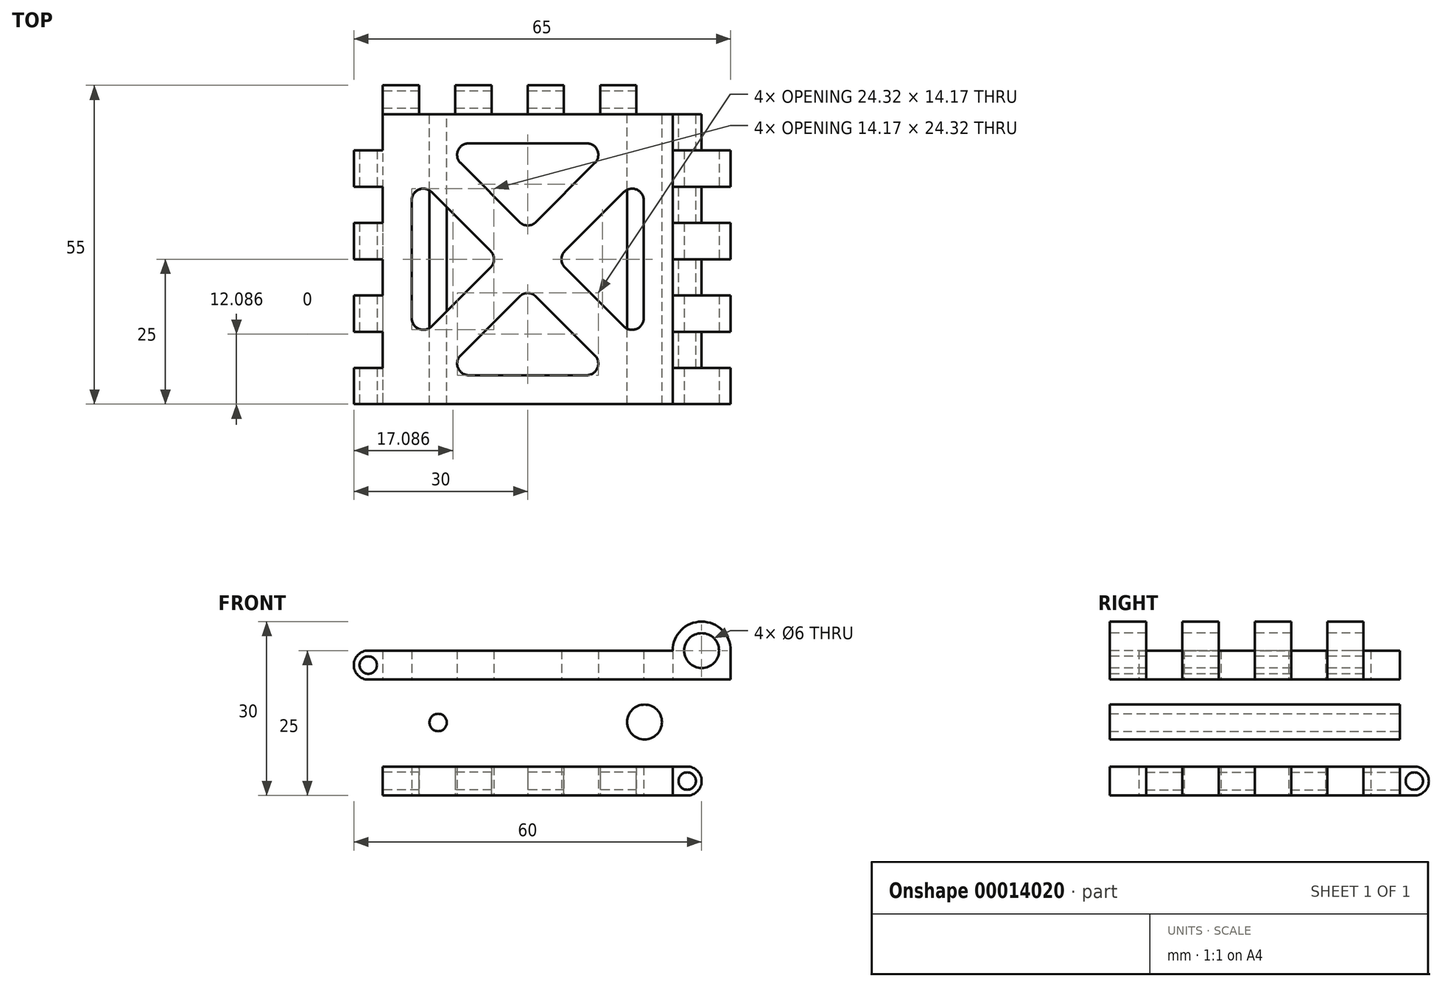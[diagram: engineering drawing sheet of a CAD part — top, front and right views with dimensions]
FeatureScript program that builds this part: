
annotation { "Feature Type Name" : "Feature", "Feature Type Description" : "" }
export const myFeature = defineFeature(function(context is Context, id is Id, definition is map)
    precondition{}
    {
        {
            var Q0;
            Q0=qCreatedBy(makeId("Top.planeOp"),FACE);
            var sketch = newSketch(context, id + "F0", { "sketchPlane" : qUnion([Q0])});
            skLineSegment(sketch, "E0.bottom", {"start": v(-25, 25) * mm, "end": v(25, 25) * mm});
            skLineSegment(sketch, "E0.top", {"start": v(-25, -25) * mm, "end": v(25, -25) * mm});
            skLineSegment(sketch, "E0.left", {"start": v(-25, 25) * mm, "end": v(-25, -25) * mm});
            skLineSegment(sketch, "E0.right", {"start": v(25, 25) * mm, "end": v(25, -25) * mm});
            skLineSegment(sketch, "E1", {"start": v(-25, 25) * mm, "end": v(25, -25) * mm, "construction": true});
            skLineSegment(sketch, "E2.top", {"start": v(-25, 35) * mm, "end": v(-18.75, 35) * mm});
            skLineSegment(sketch, "E2.left", {"start": v(-25, 25) * mm, "end": v(-25, 35) * mm});
            skLineSegment(sketch, "E2.right", {"start": v(25, 25) * mm, "end": v(25, 35) * mm});
            skLineSegment(sketch, "E3.bottom", {"start": v(25, 25) * mm, "end": v(35, 25) * mm});
            skLineSegment(sketch, "E3.top", {"start": v(25, -25) * mm, "end": v(35, -25) * mm});
            skLineSegment(sketch, "E3.right", {"start": v(35, 25) * mm, "end": v(35, 18.75) * mm});
            skLineSegment(sketch, "E4.bottom", {"start": v(25, -25) * mm, "end": v(-25, -25) * mm});
            skLineSegment(sketch, "E4.top", {"start": v(25, -35) * mm, "end": v(18.75, -35) * mm});
            skLineSegment(sketch, "E4.left", {"start": v(25, -25) * mm, "end": v(25, -35) * mm});
            skLineSegment(sketch, "E4.right", {"start": v(-25, -25) * mm, "end": v(-25, -35) * mm});
            skLineSegment(sketch, "E5", {"start": v(0, 35) * mm, "end": v(6.25, 35) * mm});
            skLineSegment(sketch, "E6", {"start": v(-12.5, 35) * mm, "end": v(-6.25, 35) * mm});
            skLineSegment(sketch, "E7", {"start": v(-18.75, 35) * mm, "end": v(-12.5, 35) * mm});
            skLineSegment(sketch, "E8", {"start": v(-6.25, 35) * mm, "end": v(0, 35) * mm});
            skLineSegment(sketch, "E9", {"start": v(12.5, 35) * mm, "end": v(18.75, 35) * mm});
            skLineSegment(sketch, "E10", {"start": v(6.25, 35) * mm, "end": v(12.5, 35) * mm});
            skLineSegment(sketch, "E11", {"start": v(18.75, 35) * mm, "end": v(25, 35) * mm});
            skLineSegment(sketch, "E12", {"start": v(35, 0) * mm, "end": v(35, -6.25) * mm});
            skLineSegment(sketch, "E13", {"start": v(35, 12.5) * mm, "end": v(35, 6.25) * mm});
            skLineSegment(sketch, "E14", {"start": v(35, 18.75) * mm, "end": v(35, 12.5) * mm});
            skLineSegment(sketch, "E15", {"start": v(35, 6.25) * mm, "end": v(35, 0) * mm});
            skLineSegment(sketch, "E16", {"start": v(35, -12.5) * mm, "end": v(35, -18.75) * mm});
            skLineSegment(sketch, "E17", {"start": v(35, -6.25) * mm, "end": v(35, -12.5) * mm});
            skLineSegment(sketch, "E18", {"start": v(35, -18.75) * mm, "end": v(35, -25) * mm});
            skLineSegment(sketch, "E19", {"start": v(0, -35) * mm, "end": v(-6.25, -35) * mm});
            skLineSegment(sketch, "E20", {"start": v(12.5, -35) * mm, "end": v(6.25, -35) * mm});
            skLineSegment(sketch, "E21", {"start": v(-12.5, -35) * mm, "end": v(-18.75, -35) * mm});
            skLineSegment(sketch, "E22", {"start": v(-18.75, -35) * mm, "end": v(-25, -35) * mm});
            skLineSegment(sketch, "E23", {"start": v(-6.25, -35) * mm, "end": v(-12.5, -35) * mm});
            skLineSegment(sketch, "E24", {"start": v(6.25, -35) * mm, "end": v(0, -35) * mm});
            skLineSegment(sketch, "E25", {"start": v(18.75, -35) * mm, "end": v(12.5, -35) * mm});
            skLineSegment(sketch, "E26.bottom", {"start": v(-25, 25) * mm, "end": v(-35, 25) * mm});
            skLineSegment(sketch, "E26.top", {"start": v(-25, -25) * mm, "end": v(-35, -25) * mm});
            skLineSegment(sketch, "E26.right", {"start": v(-35, 25) * mm, "end": v(-35, 18.75) * mm});
            skLineSegment(sketch, "E27", {"start": v(-35, 0) * mm, "end": v(-35, -6.25) * mm});
            skLineSegment(sketch, "E28", {"start": v(-35, 12.5) * mm, "end": v(-35, 6.25) * mm});
            skLineSegment(sketch, "E29", {"start": v(-35, -12.5) * mm, "end": v(-35, -18.75) * mm});
            skLineSegment(sketch, "E30", {"start": v(-35, -18.75) * mm, "end": v(-35, -25) * mm});
            skLineSegment(sketch, "E31", {"start": v(-35, -6.25) * mm, "end": v(-35, -12.5) * mm});
            skLineSegment(sketch, "E32", {"start": v(-35, 6.25) * mm, "end": v(-35, 0) * mm});
            skLineSegment(sketch, "E33", {"start": v(-35, 18.75) * mm, "end": v(-35, 12.5) * mm});
            skLineSegment(sketch, "E34", {"start": v(-18.75, 35) * mm, "end": v(-18.75, 25) * mm});
            skLineSegment(sketch, "E35", {"start": v(-12.5, -35) * mm, "end": v(-12.5, -25) * mm});
            skLineSegment(sketch, "E36", {"start": v(-6.25, 35) * mm, "end": v(-6.25, 25) * mm});
            skLineSegment(sketch, "E37", {"start": v(0, -35) * mm, "end": v(0, -25) * mm});
            skLineSegment(sketch, "E38", {"start": v(6.25, 35) * mm, "end": v(6.25, 25) * mm});
            skLineSegment(sketch, "E39", {"start": v(12.5, -35) * mm, "end": v(12.5, -25) * mm});
            skLineSegment(sketch, "E40", {"start": v(18.75, 35) * mm, "end": v(18.75, 25) * mm});
            skLineSegment(sketch, "E41", {"start": v(35, -18.75) * mm, "end": v(25, -18.75) * mm});
            skLineSegment(sketch, "E42", {"start": v(-35, -12.5) * mm, "end": v(-25, -12.5) * mm});
            skLineSegment(sketch, "E43", {"start": v(35, -6.25) * mm, "end": v(25, -6.25) * mm});
            skLineSegment(sketch, "E44", {"start": v(-35, 0) * mm, "end": v(-25, 0) * mm});
            skLineSegment(sketch, "E45", {"start": v(35, 6.25) * mm, "end": v(25, 6.25) * mm});
            skLineSegment(sketch, "E46", {"start": v(-35, 12.5) * mm, "end": v(-25, 12.5) * mm});
            skLineSegment(sketch, "E47", {"start": v(35, 18.75) * mm, "end": v(25, 18.75) * mm});
            skLineSegment(sketch, "E48.trimOffspring", {"start": v(-25, 18.75) * mm, "end": v(-35, 18.75) * mm});
            skLineSegment(sketch, "E49.trimOffspring", {"start": v(25, 12.5) * mm, "end": v(35, 12.5) * mm});
            skLineSegment(sketch, "E50.trimOffspring", {"start": v(25, 0) * mm, "end": v(35, 0) * mm});
            skLineSegment(sketch, "E51.trimOffspring", {"start": v(25, -12.5) * mm, "end": v(35, -12.5) * mm});
            skLineSegment(sketch, "E52.trimOffspring", {"start": v(18.75, -25) * mm, "end": v(18.75, -35) * mm});
            skLineSegment(sketch, "E53.trimOffspring", {"start": v(6.25, -25) * mm, "end": v(6.25, -35) * mm});
            skLineSegment(sketch, "E54.trimOffspring", {"start": v(-6.25, -25) * mm, "end": v(-6.25, -35) * mm});
            skLineSegment(sketch, "E55.trimOffspring", {"start": v(-18.75, -25) * mm, "end": v(-18.75, -35) * mm});
            skLineSegment(sketch, "E56.trimOffspring", {"start": v(-25, -18.75) * mm, "end": v(-35, -18.75) * mm});
            skLineSegment(sketch, "E57.trimOffspring", {"start": v(-25, -6.25) * mm, "end": v(-35, -6.25) * mm});
            skLineSegment(sketch, "E58.trimOffspring", {"start": v(-25, 6.25) * mm, "end": v(-35, 6.25) * mm});
            skLineSegment(sketch, "E59.trimOffspring", {"start": v(-12.5, 25) * mm, "end": v(-12.5, 35) * mm});
            skLineSegment(sketch, "E60.trimOffspring", {"start": v(0, 25) * mm, "end": v(0, 35) * mm});
            skLineSegment(sketch, "E61.trimOffspring", {"start": v(12.5, 25) * mm, "end": v(12.5, 35) * mm});
            skLineSegment(sketch, "E62", {"start": v(-25, -25) * mm, "end": v(25, 25) * mm, "construction": true});
            skLineSegment(sketch, "E63", {"start": v(-20, 10.17) * mm, "end": v(-20, -10.17) * mm});
            skLineSegment(sketch, "E64", {"start": v(-16.59, -11.59) * mm, "end": v(-6.41, -1.41) * mm});
            skLineSegment(sketch, "E65", {"start": v(-6.41, 1.41) * mm, "end": v(-16.59, 11.59) * mm});
            skCircle(sketch, "E66", {"center": v(0, 0) * mm, "radius": 5 * mm, "construction": true});
            skCircle(sketch, "E67", {"center": v(0, 0) * mm, "radius": 20 * mm, "construction": true});
            skLineSegment(sketch, "E68", {"start": v(-25, 0) * mm, "end": v(-20, 0) * mm, "construction": true});
            skLineSegment(sketch, "E69", {"start": v(0, 0) * mm, "end": v(-5, 0) * mm, "construction": true});
            skLineSegment(sketch, "E70", {"start": v(-10.17, 20) * mm, "end": v(10.17, 20) * mm});
            skLineSegment(sketch, "E71", {"start": v(11.59, 16.59) * mm, "end": v(1.41, 6.41) * mm});
            skLineSegment(sketch, "E72", {"start": v(-1.41, 6.41) * mm, "end": v(-11.59, 16.59) * mm});
            skLineSegment(sketch, "E73", {"start": v(20, 10.17) * mm, "end": v(20, -10.17) * mm});
            skLineSegment(sketch, "E74", {"start": v(16.59, -11.59) * mm, "end": v(6.41, -1.41) * mm});
            skLineSegment(sketch, "E75", {"start": v(6.41, 1.41) * mm, "end": v(16.59, 11.59) * mm});
            skLineSegment(sketch, "E76", {"start": v(-10.17, -20) * mm, "end": v(10.17, -20) * mm});
            skLineSegment(sketch, "E77", {"start": v(11.59, -16.59) * mm, "end": v(1.41, -6.41) * mm});
            skLineSegment(sketch, "E78", {"start": v(-1.41, -6.41) * mm, "end": v(-11.59, -16.59) * mm});
            skPoint(sketch, "E79.visualSharp", {"position": v(-15, 20) * mm});
            skArc(sketch, "E79.filletArc", {"start": v(-10.17, 20) * mm, "mid": v(-12.02, 18.77) * mm, "end": v(-11.59, 16.59) * mm});
            skPoint(sketch, "E80.visualSharp", {"position": v(15, 20) * mm});
            skArc(sketch, "E80.filletArc", {"start": v(11.59, 16.59) * mm, "mid": v(12.02, 18.77) * mm, "end": v(10.17, 20) * mm});
            skPoint(sketch, "E81.visualSharp", {"position": v(0, 5) * mm});
            skArc(sketch, "E81.filletArc", {"start": v(-1.41, 6.41) * mm, "mid": v(0, 5.83) * mm, "end": v(1.41, 6.41) * mm});
            skPoint(sketch, "E82.visualSharp", {"position": v(20, 15) * mm});
            skArc(sketch, "E82.filletArc", {"start": v(20, 10.17) * mm, "mid": v(18.77, 12.02) * mm, "end": v(16.59, 11.59) * mm});
            skPoint(sketch, "E83.visualSharp", {"position": v(20, -15) * mm});
            skArc(sketch, "E83.filletArc", {"start": v(16.59, -11.59) * mm, "mid": v(18.77, -12.02) * mm, "end": v(20, -10.17) * mm});
            skPoint(sketch, "E84.visualSharp", {"position": v(5, 0) * mm});
            skArc(sketch, "E84.filletArc", {"start": v(6.41, 1.41) * mm, "mid": v(5.83, 0) * mm, "end": v(6.41, -1.41) * mm});
            skPoint(sketch, "E85.visualSharp", {"position": v(0, -5) * mm});
            skArc(sketch, "E85.filletArc", {"start": v(1.41, -6.41) * mm, "mid": v(0, -5.83) * mm, "end": v(-1.41, -6.41) * mm});
            skPoint(sketch, "E86.visualSharp", {"position": v(15, -20) * mm});
            skArc(sketch, "E86.filletArc", {"start": v(10.17, -20) * mm, "mid": v(12.02, -18.77) * mm, "end": v(11.59, -16.59) * mm});
            skPoint(sketch, "E87.visualSharp", {"position": v(-15, -20) * mm});
            skArc(sketch, "E87.filletArc", {"start": v(-11.59, -16.59) * mm, "mid": v(-12.02, -18.77) * mm, "end": v(-10.17, -20) * mm});
            skPoint(sketch, "E88.visualSharp", {"position": v(-20, -15) * mm});
            skArc(sketch, "E88.filletArc", {"start": v(-20, -10.17) * mm, "mid": v(-18.77, -12.02) * mm, "end": v(-16.59, -11.59) * mm});
            skPoint(sketch, "E89.visualSharp", {"position": v(-5, 0) * mm});
            skArc(sketch, "E89.filletArc", {"start": v(-6.41, -1.41) * mm, "mid": v(-5.83, 0) * mm, "end": v(-6.41, 1.41) * mm});
            skPoint(sketch, "E90.visualSharp", {"position": v(-20, 15) * mm});
            skArc(sketch, "E90.filletArc", {"start": v(-16.59, 11.59) * mm, "mid": v(-18.77, 12.02) * mm, "end": v(-20, 10.17) * mm});
            skSolve(sketch);
        }
        {
            var Q0;
            Q0=makeQuery(id+"F0.imprint","IMPRINT",FACE,{"disambiguationData":[TD([[makeQuery(id+"F0.imprint","IMPRINT",EDGE,{"derivedFrom":sQuery(id+"F0.wireOp",EDGE,"E63")}),-1.0]])]});
            var Q1;
            Q1=makeQuery(id+"F0.imprint","IMPRINT",FACE,{"disambiguationData":[TD([[makeQuery(id+"F0.imprint","IMPRINT",EDGE,{"derivedFrom":sQuery(id+"F0.wireOp",EDGE,"E2.top")}),-1.0]])]});
            var Q2;
            Q2=makeQuery(id+"F0.imprint","IMPRINT",FACE,{"disambiguationData":[TD([[makeQuery(id+"F0.imprint","IMPRINT",EDGE,{"derivedFrom":sQuery(id+"F0.wireOp",EDGE,"E7")}),-1.0]])]});
            var Q3;
            Q3=makeQuery(id+"F0.imprint","IMPRINT",FACE,{"disambiguationData":[TD([[makeQuery(id+"F0.imprint","IMPRINT",EDGE,{"derivedFrom":sQuery(id+"F0.wireOp",EDGE,"E6")}),-1.0]])]});
            var Q4;
            Q4=makeQuery(id+"F0.imprint","IMPRINT",FACE,{"disambiguationData":[TD([[makeQuery(id+"F0.imprint","IMPRINT",EDGE,{"derivedFrom":sQuery(id+"F0.wireOp",EDGE,"E8")}),-1.0]])]});
            var Q5;
            Q5=makeQuery(id+"F0.imprint","IMPRINT",FACE,{"disambiguationData":[TD([[makeQuery(id+"F0.imprint","IMPRINT",EDGE,{"derivedFrom":sQuery(id+"F0.wireOp",EDGE,"E5")}),-1.0]])]});
            var Q6;
            Q6=makeQuery(id+"F0.imprint","IMPRINT",FACE,{"disambiguationData":[TD([[makeQuery(id+"F0.imprint","IMPRINT",EDGE,{"derivedFrom":sQuery(id+"F0.wireOp",EDGE,"E10")}),-1.0]])]});
            var Q7;
            Q7=makeQuery(id+"F0.imprint","IMPRINT",FACE,{"disambiguationData":[TD([[makeQuery(id+"F0.imprint","IMPRINT",EDGE,{"derivedFrom":sQuery(id+"F0.wireOp",EDGE,"E9")}),-1.0]])]});
            var Q8;
            {var subQ1=sQuery(id+"F0.wireOp",EDGE,"E2.right");Q8=makeQuery(id+"F0.imprint","IMPRINT",FACE,{"disambiguationData":[TD([[makeQuery(id+"F0.imprint","IMPRINT",EDGE,{"derivedFrom":subQ1}),1.0]])]});}
            var Q9;
            {var subQ2=sQuery(id+"F0.wireOp",EDGE,"E3.bottom");Q9=makeQuery(id+"F0.imprint","IMPRINT",FACE,{"disambiguationData":[TD([[makeQuery(id+"F0.imprint","IMPRINT",EDGE,{"derivedFrom":subQ2}),-1.0]])]});}
            var Q10;
            Q10=makeQuery(id+"F0.imprint","IMPRINT",FACE,{"disambiguationData":[TD([[makeQuery(id+"F0.imprint","IMPRINT",EDGE,{"derivedFrom":sQuery(id+"F0.wireOp",EDGE,"E14")}),-1.0]])]});
            var Q11;
            Q11=makeQuery(id+"F0.imprint","IMPRINT",FACE,{"disambiguationData":[TD([[makeQuery(id+"F0.imprint","IMPRINT",EDGE,{"derivedFrom":sQuery(id+"F0.wireOp",EDGE,"E13")}),-1.0]])]});
            var Q12;
            Q12=makeQuery(id+"F0.imprint","IMPRINT",FACE,{"disambiguationData":[TD([[makeQuery(id+"F0.imprint","IMPRINT",EDGE,{"derivedFrom":sQuery(id+"F0.wireOp",EDGE,"E15")}),-1.0]])]});
            var Q13;
            Q13=makeQuery(id+"F0.imprint","IMPRINT",FACE,{"disambiguationData":[TD([[makeQuery(id+"F0.imprint","IMPRINT",EDGE,{"derivedFrom":sQuery(id+"F0.wireOp",EDGE,"E12")}),-1.0]])]});
            var Q14;
            Q14=makeQuery(id+"F0.imprint","IMPRINT",FACE,{"disambiguationData":[TD([[makeQuery(id+"F0.imprint","IMPRINT",EDGE,{"derivedFrom":sQuery(id+"F0.wireOp",EDGE,"E17")}),-1.0]])]});
            var Q15;
            Q15=makeQuery(id+"F0.imprint","IMPRINT",FACE,{"disambiguationData":[TD([[makeQuery(id+"F0.imprint","IMPRINT",EDGE,{"derivedFrom":sQuery(id+"F0.wireOp",EDGE,"E16")}),-1.0]])]});
            var Q16;
            {var subQ2=sQuery(id+"F0.wireOp",EDGE,"E3.top");Q16=makeQuery(id+"F0.imprint","IMPRINT",FACE,{"disambiguationData":[TD([[makeQuery(id+"F0.imprint","IMPRINT",EDGE,{"derivedFrom":subQ2}),1.0]])]});}
            extrude(context, id + "F1", {"entities" : qUnion([Q0, Q1, Q2, Q3, Q4, Q5, Q6, Q7, Q8, Q9, Q10, Q11, Q12, Q13, Q14, Q15, Q16]), "depth" : 5 * mm});
        }
        {
            var Q0;
            Q0=makeQuery(id+"F1.opExtrude","SWEPT_FACE",FACE,{"disambiguationData":[OSD([sQuery(id+"F0.wireOp",EDGE,"E2.left"),sQuery(id+"F0.wireOp",EDGE,"E0.left")])]});
            var sketch = newSketch(context, id + "F2", { "sketchPlane" : qUnion([Q0])});
            skLineSegment(sketch, "E91.0.0", {"start": v(-35, 0) * mm, "end": v(25, 0) * mm});
            skLineSegment(sketch, "E91.0.1", {"start": v(25, 0) * mm, "end": v(25, 5) * mm});
            skLineSegment(sketch, "E91.0.2", {"start": v(25, 5) * mm, "end": v(-35, 5) * mm});
            skLineSegment(sketch, "E91.0.3", {"start": v(-35, 5) * mm, "end": v(-35, 0) * mm});
            skLineSegment(sketch, "E92.0", {"start": v(-25, 5) * mm, "end": v(-25, 0) * mm});
            skCircle(sketch, "E93", {"center": v(-27.5, 2.5) * mm, "radius": 2.5 * mm});
            skCircle(sketch, "E94", {"center": v(-27.5, 2.5) * mm, "radius": 1.5 * mm});
            skSolve(sketch);
        }
        {
            var Q0;
            {var subQ5=sQuery(id+"F2.wireOp",EDGE,"E91.0.3");Q0=makeQuery(id+"F2.imprint","IMPRINT",FACE,{"disambiguationData":[TD([[makeQuery(id+"F2.imprint","IMPRINT",EDGE,{"derivedFrom":subQ5}),1.0]])]});}
            var Q1;
            Q1=makeQuery(id+"F2.imprint","IMPRINT",FACE,{"disambiguationData":[TD([[makeQuery(id+"F2.imprint","IMPRINT",EDGE,{"derivedFrom":sQuery(id+"F2.wireOp",EDGE,"E94")}),1.0]])]});
            var Q2;
            Q2=makeQuery(id+"F1.opExtrude","SWEPT_FACE",FACE,{"disambiguationData":[OSD([sQuery(id+"F0.wireOp",EDGE,"E2.right")])]});
            extrude(context, id + "F3", {"entities" : qUnion([Q0, Q1]), "operationType" : NewBodyOperationType.REMOVE, "endBound" : BoundingType.UP_TO_SURFACE, "oppositeDirection" : true, "endBoundEntityFace" : qUnion([Q2]), "depth" : 25 * mm});
        }
        {
            var Q0;
            Q0=makeQuery(id+"F0.imprint","IMPRINT",FACE,{"disambiguationData":[TD([[makeQuery(id+"F0.imprint","IMPRINT",EDGE,{"derivedFrom":sQuery(id+"F0.wireOp",EDGE,"E7")}),-1.0]])]});
            var Q1;
            Q1=makeQuery(id+"F0.imprint","IMPRINT",FACE,{"disambiguationData":[TD([[makeQuery(id+"F0.imprint","IMPRINT",EDGE,{"derivedFrom":sQuery(id+"F0.wireOp",EDGE,"E8")}),-1.0]])]});
            var Q2;
            Q2=makeQuery(id+"F0.imprint","IMPRINT",FACE,{"disambiguationData":[TD([[makeQuery(id+"F0.imprint","IMPRINT",EDGE,{"derivedFrom":sQuery(id+"F0.wireOp",EDGE,"E10")}),-1.0]])]});
            var Q3;
            {var subQ1=sQuery(id+"F0.wireOp",EDGE,"E2.right");Q3=makeQuery(id+"F0.imprint","IMPRINT",FACE,{"disambiguationData":[TD([[makeQuery(id+"F0.imprint","IMPRINT",EDGE,{"derivedFrom":subQ1}),1.0]])]});}
            var Q4;
            Q4=makeQuery(id+"F1.opExtrude","CAP_FACE",FACE,{"disambiguationData":[OSD([sQuery(id+"F0.wireOp",EDGE,"E2.top"),sQuery(id+"F0.wireOp",EDGE,"E2.left"),sQuery(id+"F0.wireOp",EDGE,"E2.right"),sQuery(id+"F0.wireOp",EDGE,"E3.bottom"),sQuery(id+"F0.wireOp",EDGE,"E3.top"),sQuery(id+"F0.wireOp",EDGE,"E3.right"),sQuery(id+"F0.wireOp",EDGE,"E4.bottom"),sQuery(id+"F0.wireOp",EDGE,"E5"),sQuery(id+"F0.wireOp",EDGE,"E6"),sQuery(id+"F0.wireOp",EDGE,"E7"),sQuery(id+"F0.wireOp",EDGE,"E8"),sQuery(id+"F0.wireOp",EDGE,"E9"),sQuery(id+"F0.wireOp",EDGE,"E10"),sQuery(id+"F0.wireOp",EDGE,"E11"),sQuery(id+"F0.wireOp",EDGE,"E12"),sQuery(id+"F0.wireOp",EDGE,"E13"),sQuery(id+"F0.wireOp",EDGE,"E14"),sQuery(id+"F0.wireOp",EDGE,"E15"),sQuery(id+"F0.wireOp",EDGE,"E16"),sQuery(id+"F0.wireOp",EDGE,"E17"),sQuery(id+"F0.wireOp",EDGE,"E18"),sQuery(id+"F0.wireOp",EDGE,"E0.left"),sQuery(id+"F0.wireOp",EDGE,"E63"),sQuery(id+"F0.wireOp",EDGE,"E64"),sQuery(id+"F0.wireOp",EDGE,"E65"),sQuery(id+"F0.wireOp",EDGE,"E70"),sQuery(id+"F0.wireOp",EDGE,"E71"),sQuery(id+"F0.wireOp",EDGE,"E72"),sQuery(id+"F0.wireOp",EDGE,"E73"),sQuery(id+"F0.wireOp",EDGE,"E74"),sQuery(id+"F0.wireOp",EDGE,"E75"),sQuery(id+"F0.wireOp",EDGE,"E76"),sQuery(id+"F0.wireOp",EDGE,"E77"),sQuery(id+"F0.wireOp",EDGE,"E78"),sQuery(id+"F0.wireOp",EDGE,"E79.filletArc"),sQuery(id+"F0.wireOp",EDGE,"E80.filletArc"),sQuery(id+"F0.wireOp",EDGE,"E81.filletArc"),sQuery(id+"F0.wireOp",EDGE,"E82.filletArc"),sQuery(id+"F0.wireOp",EDGE,"E83.filletArc"),sQuery(id+"F0.wireOp",EDGE,"E84.filletArc"),sQuery(id+"F0.wireOp",EDGE,"E85.filletArc"),sQuery(id+"F0.wireOp",EDGE,"E86.filletArc"),sQuery(id+"F0.wireOp",EDGE,"E87.filletArc"),sQuery(id+"F0.wireOp",EDGE,"E88.filletArc"),sQuery(id+"F0.wireOp",EDGE,"E89.filletArc"),sQuery(id+"F0.wireOp",EDGE,"E90.filletArc")])],"isStart":false});
            extrude(context, id + "F4", {"entities" : qUnion([Q0, Q1, Q2, Q3]), "operationType" : NewBodyOperationType.REMOVE, "endBound" : BoundingType.UP_TO_SURFACE, "endBoundEntityFace" : qUnion([Q4]), "depth" : 25 * mm});
        }
        {
            var Q0;
            {var subQ0=sQuery(id+"F0.wireOp",EDGE,"E3.bottom");var subQ1=sQuery(id+"F0.wireOp",EDGE,"E0.bottom");Q0=makeQuery(id+"F4.boolean.opBoolean","MERGE",FACE,{"derivedFrom":[makeQuery(id+"F1.opExtrude","SWEPT_FACE",FACE,{"disambiguationData":[OSD([subQ0])]}),makeQuery(id+"F4.opExtrude","SWEPT_FACE",FACE,{"disambiguationData":[OSD([subQ1]),TDD([makeQuery(id+"F0.imprint","IMPRINT",EDGE,{"disambiguationData":[TD([[makeQuery(id+"F0.imprint","INTERSECT",VERTEX,{"derivedFrom":[subQ1,sQuery(id+"F0.wireOp",EDGE,"E40")]}),-1.0]])],"derivedFrom":subQ1})])]})]});}
            var sketch = newSketch(context, id + "F5", { "sketchPlane" : qUnion([Q0])});
            skLineSegment(sketch, "E95.0", {"start": v(25, 0) * mm, "end": v(-25, 0) * mm});
            skLineSegment(sketch, "E95.1", {"start": v(25, 0) * mm, "end": v(-25, 0) * mm});
            skLineSegment(sketch, "E95.4", {"start": v(25, 0) * mm, "end": v(-25, 0) * mm});
            skLineSegment(sketch, "E95.5", {"start": v(25, 0) * mm, "end": v(-25, 0) * mm});
            skLineSegment(sketch, "E95.6", {"start": v(25, 0) * mm, "end": v(18.75, 0) * mm});
            skLineSegment(sketch, "E95.9", {"start": v(-25, 0) * mm, "end": v(-35, 0) * mm});
            skLineSegment(sketch, "E95.10", {"start": v(-25, 0) * mm, "end": v(-35, 0) * mm});
            skLineSegment(sketch, "E95.13", {"start": v(-25, 0) * mm, "end": v(25, 0) * mm});
            skLineSegment(sketch, "E95.14", {"start": v(-25, 0) * mm, "end": v(-18.75, 0) * mm});
            skLineSegment(sketch, "E95.17", {"start": v(0, 0) * mm, "end": v(-6.25, 0) * mm});
            skLineSegment(sketch, "E95.18", {"start": v(12.5, 0) * mm, "end": v(6.25, 0) * mm});
            skLineSegment(sketch, "E95.19", {"start": v(18.75, 0) * mm, "end": v(12.5, 0) * mm});
            skLineSegment(sketch, "E95.20", {"start": v(6.25, 0) * mm, "end": v(0, 0) * mm});
            skLineSegment(sketch, "E95.21", {"start": v(-12.5, 0) * mm, "end": v(-18.75, 0) * mm});
            skLineSegment(sketch, "E95.22", {"start": v(-6.25, 0) * mm, "end": v(-12.5, 0) * mm});
            skLineSegment(sketch, "E95.23", {"start": v(-18.75, 0) * mm, "end": v(-25, 0) * mm});
            skLineSegment(sketch, "E95.31", {"start": v(0, 0) * mm, "end": v(6.25, 0) * mm});
            skLineSegment(sketch, "E95.32", {"start": v(-12.5, 0) * mm, "end": v(-6.25, 0) * mm});
            skLineSegment(sketch, "E95.33", {"start": v(12.5, 0) * mm, "end": v(18.75, 0) * mm});
            skLineSegment(sketch, "E95.34", {"start": v(18.75, 0) * mm, "end": v(25, 0) * mm});
            skLineSegment(sketch, "E95.35", {"start": v(6.25, 0) * mm, "end": v(12.5, 0) * mm});
            skLineSegment(sketch, "E95.36", {"start": v(-6.25, 0) * mm, "end": v(0, 0) * mm});
            skLineSegment(sketch, "E95.37", {"start": v(-18.75, 0) * mm, "end": v(-12.5, 0) * mm});
            skLineSegment(sketch, "E95.38", {"start": v(25, 0) * mm, "end": v(35, 0) * mm});
            skLineSegment(sketch, "E95.39", {"start": v(25, 0) * mm, "end": v(35, 0) * mm});
            skLineSegment(sketch, "E95.56", {"start": v(-35, 0) * mm, "end": v(-25, 0) * mm});
            skLineSegment(sketch, "E95.57", {"start": v(35, 0) * mm, "end": v(25, 0) * mm});
            skLineSegment(sketch, "E95.58", {"start": v(-35, 0) * mm, "end": v(-25, 0) * mm});
            skLineSegment(sketch, "E95.59", {"start": v(35, 0) * mm, "end": v(25, 0) * mm});
            skLineSegment(sketch, "E95.60", {"start": v(-35, 0) * mm, "end": v(-25, 0) * mm});
            skLineSegment(sketch, "E95.61", {"start": v(35, 0) * mm, "end": v(25, 0) * mm});
            skLineSegment(sketch, "E95.62", {"start": v(-35, 0) * mm, "end": v(-25, 0) * mm});
            skLineSegment(sketch, "E95.63", {"start": v(25, 0) * mm, "end": v(35, 0) * mm});
            skLineSegment(sketch, "E95.64", {"start": v(-25, 0) * mm, "end": v(-35, 0) * mm});
            skLineSegment(sketch, "E95.65", {"start": v(-25, 0) * mm, "end": v(-35, 0) * mm});
            skLineSegment(sketch, "E95.66", {"start": v(-25, 0) * mm, "end": v(-35, 0) * mm});
            skLineSegment(sketch, "E95.71", {"start": v(25, 0) * mm, "end": v(35, 0) * mm});
            skLineSegment(sketch, "E95.72", {"start": v(25, 0) * mm, "end": v(35, 0) * mm});
            skLineSegment(sketch, "E95.73", {"start": v(25, 0) * mm, "end": v(35, 0) * mm});
            skLineSegment(sketch, "E95.77", {"start": v(25, 0) * mm, "end": v(-25, 0) * mm});
            skLineSegment(sketch, "E95.79", {"start": v(16.59, 0) * mm, "end": v(6.41, 0) * mm});
            skLineSegment(sketch, "E95.80", {"start": v(6.41, 0) * mm, "end": v(16.59, 0) * mm});
            skLineSegment(sketch, "E95.81", {"start": v(-5, 0) * mm, "end": v(5, 0) * mm});
            skLineSegment(sketch, "E95.82", {"start": v(-20, 0) * mm, "end": v(20, 0) * mm});
            skLineSegment(sketch, "E95.83", {"start": v(25, 0) * mm, "end": v(20, 0) * mm});
            skLineSegment(sketch, "E95.84", {"start": v(0, 0) * mm, "end": v(5, 0) * mm});
            skLineSegment(sketch, "E95.85", {"start": v(10.17, 0) * mm, "end": v(-10.17, 0) * mm});
            skLineSegment(sketch, "E95.86", {"start": v(-11.59, 0) * mm, "end": v(-1.41, 0) * mm});
            skLineSegment(sketch, "E95.87", {"start": v(1.41, 0) * mm, "end": v(11.59, 0) * mm});
            skLineSegment(sketch, "E95.89", {"start": v(-16.59, 0) * mm, "end": v(-6.41, 0) * mm});
            skLineSegment(sketch, "E95.90", {"start": v(-6.41, 0) * mm, "end": v(-16.59, 0) * mm});
            skLineSegment(sketch, "E95.91", {"start": v(10.17, 0) * mm, "end": v(-10.17, 0) * mm});
            skLineSegment(sketch, "E95.92", {"start": v(-11.59, 0) * mm, "end": v(-1.41, 0) * mm});
            skLineSegment(sketch, "E95.93", {"start": v(1.41, 0) * mm, "end": v(11.59, 0) * mm});
            skPoint(sketch, "E95.94", {"position": v(15, 0) * mm});
            skLineSegment(sketch, "E95.95", {"start": v(10.17, 0) * mm, "end": v(12.17, 0) * mm});
            skPoint(sketch, "E95.96", {"position": v(-15, 0) * mm});
            skLineSegment(sketch, "E95.97", {"start": v(-12.17, 0) * mm, "end": v(-10.17, 0) * mm});
            skPoint(sketch, "E95.98", {"position": v(0, 0) * mm});
            skLineSegment(sketch, "E95.99", {"start": v(-1.41, 0) * mm, "end": v(1.41, 0) * mm});
            skPoint(sketch, "E95.100", {"position": v(-20, 0) * mm});
            skLineSegment(sketch, "E95.101", {"start": v(-20, 0) * mm, "end": v(-16.59, 0) * mm});
            skPoint(sketch, "E95.102", {"position": v(-20, 0) * mm});
            skLineSegment(sketch, "E95.103", {"start": v(-20, 0) * mm, "end": v(-16.59, 0) * mm});
            skPoint(sketch, "E95.104", {"position": v(-5, 0) * mm});
            skLineSegment(sketch, "E95.105", {"start": v(-6.41, 0) * mm, "end": v(-5.83, 0) * mm});
            skPoint(sketch, "E95.106", {"position": v(0, 0) * mm});
            skLineSegment(sketch, "E95.107", {"start": v(-1.41, 0) * mm, "end": v(1.41, 0) * mm});
            skPoint(sketch, "E95.108", {"position": v(-15, 0) * mm});
            skLineSegment(sketch, "E95.109", {"start": v(-12.17, 0) * mm, "end": v(-10.17, 0) * mm});
            skPoint(sketch, "E95.110", {"position": v(15, 0) * mm});
            skLineSegment(sketch, "E95.111", {"start": v(10.17, 0) * mm, "end": v(12.17, 0) * mm});
            skPoint(sketch, "E95.112", {"position": v(20, 0) * mm});
            skLineSegment(sketch, "E95.113", {"start": v(16.59, 0) * mm, "end": v(20, 0) * mm});
            skPoint(sketch, "E95.114", {"position": v(5, 0) * mm});
            skLineSegment(sketch, "E95.115", {"start": v(5.83, 0) * mm, "end": v(6.41, 0) * mm});
            skPoint(sketch, "E95.116", {"position": v(20, 0) * mm});
            skLineSegment(sketch, "E95.117", {"start": v(16.59, 0) * mm, "end": v(20, 0) * mm});
            skLineSegment(sketch, "E96", {"start": v(-25, 0) * mm, "end": v(-25, 5) * mm});
            skCircle(sketch, "E97", {"center": v(-27.5, 2.5) * mm, "radius": 2.5 * mm});
            skCircle(sketch, "E98", {"center": v(-27.5, 2.5) * mm, "radius": 1.5 * mm});
            skSolve(sketch);
        }
        {
            var Q0;
            {var subQ0=sQuery(id+"F0.wireOp",EDGE,"E3.bottom");var subQ5=makeQuery(id+"F1.opExtrude","SWEPT_EDGE",EDGE,{"disambiguationData":[OSD([subQ0,sQuery(id+"F0.wireOp",EDGE,"E3.right")])]});Q0=makeQuery(id+"F5.imprint","IMPRINT",FACE,{"disambiguationData":[TD([[makeQuery(id+"F5.imprint","IMPRINT",EDGE,{"derivedFrom":subQ5}),1.0]])]});}
            var Q1;
            Q1=makeQuery(id+"F5.imprint","IMPRINT",FACE,{"disambiguationData":[TD([[makeQuery(id+"F5.imprint","IMPRINT",EDGE,{"derivedFrom":sQuery(id+"F5.wireOp",EDGE,"E98")}),1.0]])]});
            var Q2;
            Q2=makeQuery(id+"F1.opExtrude","SWEPT_FACE",FACE,{"disambiguationData":[OSD([sQuery(id+"F0.wireOp",EDGE,"E3.top"),sQuery(id+"F0.wireOp",EDGE,"E4.bottom")])]});
            extrude(context, id + "F6", {"entities" : qUnion([Q0, Q1]), "operationType" : NewBodyOperationType.REMOVE, "endBound" : BoundingType.UP_TO_SURFACE, "oppositeDirection" : true, "endBoundEntityFace" : qUnion([Q2]), "depth" : 25 * mm});
        }
        {
            var Q0;
            Q0=makeQuery(id+"F0.imprint","IMPRINT",FACE,{"disambiguationData":[TD([[makeQuery(id+"F0.imprint","IMPRINT",EDGE,{"derivedFrom":sQuery(id+"F0.wireOp",EDGE,"E14")}),-1.0]])]});
            var Q1;
            Q1=makeQuery(id+"F0.imprint","IMPRINT",FACE,{"disambiguationData":[TD([[makeQuery(id+"F0.imprint","IMPRINT",EDGE,{"derivedFrom":sQuery(id+"F0.wireOp",EDGE,"E15")}),-1.0]])]});
            var Q2;
            Q2=makeQuery(id+"F0.imprint","IMPRINT",FACE,{"disambiguationData":[TD([[makeQuery(id+"F0.imprint","IMPRINT",EDGE,{"derivedFrom":sQuery(id+"F0.wireOp",EDGE,"E17")}),-1.0]])]});
            var Q3;
            {var subQ2=sQuery(id+"F0.wireOp",EDGE,"E3.top");Q3=makeQuery(id+"F0.imprint","IMPRINT",FACE,{"disambiguationData":[TD([[makeQuery(id+"F0.imprint","IMPRINT",EDGE,{"derivedFrom":subQ2}),1.0]])]});}
            var Q4;
            Q4=makeQuery(id+"F1.opExtrude","CAP_FACE",FACE,{"disambiguationData":[OSD([sQuery(id+"F0.wireOp",EDGE,"E2.top"),sQuery(id+"F0.wireOp",EDGE,"E2.left"),sQuery(id+"F0.wireOp",EDGE,"E2.right"),sQuery(id+"F0.wireOp",EDGE,"E3.bottom"),sQuery(id+"F0.wireOp",EDGE,"E3.top"),sQuery(id+"F0.wireOp",EDGE,"E3.right"),sQuery(id+"F0.wireOp",EDGE,"E4.bottom"),sQuery(id+"F0.wireOp",EDGE,"E5"),sQuery(id+"F0.wireOp",EDGE,"E6"),sQuery(id+"F0.wireOp",EDGE,"E7"),sQuery(id+"F0.wireOp",EDGE,"E8"),sQuery(id+"F0.wireOp",EDGE,"E9"),sQuery(id+"F0.wireOp",EDGE,"E10"),sQuery(id+"F0.wireOp",EDGE,"E11"),sQuery(id+"F0.wireOp",EDGE,"E12"),sQuery(id+"F0.wireOp",EDGE,"E13"),sQuery(id+"F0.wireOp",EDGE,"E14"),sQuery(id+"F0.wireOp",EDGE,"E15"),sQuery(id+"F0.wireOp",EDGE,"E16"),sQuery(id+"F0.wireOp",EDGE,"E17"),sQuery(id+"F0.wireOp",EDGE,"E18"),sQuery(id+"F0.wireOp",EDGE,"E0.left"),sQuery(id+"F0.wireOp",EDGE,"E63"),sQuery(id+"F0.wireOp",EDGE,"E64"),sQuery(id+"F0.wireOp",EDGE,"E65"),sQuery(id+"F0.wireOp",EDGE,"E70"),sQuery(id+"F0.wireOp",EDGE,"E71"),sQuery(id+"F0.wireOp",EDGE,"E72"),sQuery(id+"F0.wireOp",EDGE,"E73"),sQuery(id+"F0.wireOp",EDGE,"E74"),sQuery(id+"F0.wireOp",EDGE,"E75"),sQuery(id+"F0.wireOp",EDGE,"E76"),sQuery(id+"F0.wireOp",EDGE,"E77"),sQuery(id+"F0.wireOp",EDGE,"E78"),sQuery(id+"F0.wireOp",EDGE,"E79.filletArc"),sQuery(id+"F0.wireOp",EDGE,"E80.filletArc"),sQuery(id+"F0.wireOp",EDGE,"E81.filletArc"),sQuery(id+"F0.wireOp",EDGE,"E82.filletArc"),sQuery(id+"F0.wireOp",EDGE,"E83.filletArc"),sQuery(id+"F0.wireOp",EDGE,"E84.filletArc"),sQuery(id+"F0.wireOp",EDGE,"E85.filletArc"),sQuery(id+"F0.wireOp",EDGE,"E86.filletArc"),sQuery(id+"F0.wireOp",EDGE,"E87.filletArc"),sQuery(id+"F0.wireOp",EDGE,"E88.filletArc"),sQuery(id+"F0.wireOp",EDGE,"E89.filletArc"),sQuery(id+"F0.wireOp",EDGE,"E90.filletArc")])],"isStart":false});
            extrude(context, id + "F7", {"entities" : qUnion([Q0, Q1, Q2, Q3]), "operationType" : NewBodyOperationType.REMOVE, "endBound" : BoundingType.UP_TO_SURFACE, "endBoundEntityFace" : qUnion([Q4]), "depth" : 25 * mm});
        }
        {
            var Q0;
            Q0=makeQuery(id+"F0.imprint","IMPRINT",FACE,{"disambiguationData":[TD([[makeQuery(id+"F0.imprint","IMPRINT",EDGE,{"derivedFrom":sQuery(id+"F0.wireOp",EDGE,"E63")}),-1.0]])]});
            var Q1;
            {var subQ2=sQuery(id+"F0.wireOp",EDGE,"E26.top");Q1=makeQuery(id+"F0.imprint","IMPRINT",FACE,{"disambiguationData":[TD([[makeQuery(id+"F0.imprint","IMPRINT",EDGE,{"derivedFrom":subQ2}),-1.0]])]});}
            var Q2;
            Q2=makeQuery(id+"F0.imprint","IMPRINT",FACE,{"disambiguationData":[TD([[makeQuery(id+"F0.imprint","IMPRINT",EDGE,{"derivedFrom":sQuery(id+"F0.wireOp",EDGE,"E29")}),1.0]])]});
            var Q3;
            Q3=makeQuery(id+"F0.imprint","IMPRINT",FACE,{"disambiguationData":[TD([[makeQuery(id+"F0.imprint","IMPRINT",EDGE,{"derivedFrom":sQuery(id+"F0.wireOp",EDGE,"E31")}),1.0]])]});
            var Q4;
            Q4=makeQuery(id+"F0.imprint","IMPRINT",FACE,{"disambiguationData":[TD([[makeQuery(id+"F0.imprint","IMPRINT",EDGE,{"derivedFrom":sQuery(id+"F0.wireOp",EDGE,"E27")}),1.0]])]});
            var Q5;
            Q5=makeQuery(id+"F0.imprint","IMPRINT",FACE,{"disambiguationData":[TD([[makeQuery(id+"F0.imprint","IMPRINT",EDGE,{"derivedFrom":sQuery(id+"F0.wireOp",EDGE,"E32")}),1.0]])]});
            var Q6;
            Q6=makeQuery(id+"F0.imprint","IMPRINT",FACE,{"disambiguationData":[TD([[makeQuery(id+"F0.imprint","IMPRINT",EDGE,{"derivedFrom":sQuery(id+"F0.wireOp",EDGE,"E28")}),1.0]])]});
            var Q7;
            Q7=makeQuery(id+"F0.imprint","IMPRINT",FACE,{"disambiguationData":[TD([[makeQuery(id+"F0.imprint","IMPRINT",EDGE,{"derivedFrom":sQuery(id+"F0.wireOp",EDGE,"E33")}),1.0]])]});
            var Q8;
            {var subQ2=sQuery(id+"F0.wireOp",EDGE,"E26.bottom");Q8=makeQuery(id+"F0.imprint","IMPRINT",FACE,{"disambiguationData":[TD([[makeQuery(id+"F0.imprint","IMPRINT",EDGE,{"derivedFrom":subQ2}),1.0]])]});}
            extrude(context, id + "F8", {"entities" : qUnion([Q0, Q1, Q2, Q3, Q4, Q5, Q6, Q7, Q8]), "depth" : 25 * mm, "hasSecondDirection" : true, "secondDirectionOppositeDirection" : false, "secondDirectionDepth" : 20 * mm});
        }
        {
            var Q0;
            {var subQ2=sQuery(id+"F0.wireOp",EDGE,"E3.top");Q0=makeQuery(id+"F0.imprint","IMPRINT",FACE,{"disambiguationData":[TD([[makeQuery(id+"F0.imprint","IMPRINT",EDGE,{"derivedFrom":subQ2}),1.0]])]});}
            var Q1;
            Q1=makeQuery(id+"F0.imprint","IMPRINT",FACE,{"disambiguationData":[TD([[makeQuery(id+"F0.imprint","IMPRINT",EDGE,{"derivedFrom":sQuery(id+"F0.wireOp",EDGE,"E16")}),-1.0]])]});
            var Q2;
            Q2=makeQuery(id+"F0.imprint","IMPRINT",FACE,{"disambiguationData":[TD([[makeQuery(id+"F0.imprint","IMPRINT",EDGE,{"derivedFrom":sQuery(id+"F0.wireOp",EDGE,"E17")}),-1.0]])]});
            var Q3;
            Q3=makeQuery(id+"F0.imprint","IMPRINT",FACE,{"disambiguationData":[TD([[makeQuery(id+"F0.imprint","IMPRINT",EDGE,{"derivedFrom":sQuery(id+"F0.wireOp",EDGE,"E12")}),-1.0]])]});
            var Q4;
            Q4=makeQuery(id+"F0.imprint","IMPRINT",FACE,{"disambiguationData":[TD([[makeQuery(id+"F0.imprint","IMPRINT",EDGE,{"derivedFrom":sQuery(id+"F0.wireOp",EDGE,"E15")}),-1.0]])]});
            var Q5;
            Q5=makeQuery(id+"F0.imprint","IMPRINT",FACE,{"disambiguationData":[TD([[makeQuery(id+"F0.imprint","IMPRINT",EDGE,{"derivedFrom":sQuery(id+"F0.wireOp",EDGE,"E13")}),-1.0]])]});
            var Q6;
            Q6=makeQuery(id+"F0.imprint","IMPRINT",FACE,{"disambiguationData":[TD([[makeQuery(id+"F0.imprint","IMPRINT",EDGE,{"derivedFrom":sQuery(id+"F0.wireOp",EDGE,"E14")}),-1.0]])]});
            var Q7;
            {var subQ2=sQuery(id+"F0.wireOp",EDGE,"E3.bottom");Q7=makeQuery(id+"F0.imprint","IMPRINT",FACE,{"disambiguationData":[TD([[makeQuery(id+"F0.imprint","IMPRINT",EDGE,{"derivedFrom":subQ2}),-1.0]])]});}
            extrude(context, id + "F9", {"entities" : qUnion([Q0, Q1, Q2, Q3, Q4, Q5, Q6, Q7]), "operationType" : NewBodyOperationType.ADD, "depth" : 30 * mm, "hasSecondDirection" : true, "secondDirectionOppositeDirection" : false, "secondDirectionDepth" : 20 * mm});
        }
        {
            var Q0;
            Q0=makeQuery(id+"F9.boolean.opBoolean","MERGE",FACE,{"derivedFrom":[makeQuery(id+"F8.opExtrude","SWEPT_FACE",FACE,{"disambiguationData":[OSD([sQuery(id+"F0.wireOp",EDGE,"E4.bottom"),sQuery(id+"F0.wireOp",EDGE,"E26.top")])]}),makeQuery(id+"F9.opExtrude","SWEPT_FACE",FACE,{"disambiguationData":[OSD([sQuery(id+"F0.wireOp",EDGE,"E3.top")])]})]});
            var sketch = newSketch(context, id + "F10", { "sketchPlane" : qUnion([Q0])});
            skLineSegment(sketch, "E99.0.0", {"start": v(-35, 20) * mm, "end": v(35, 20) * mm});
            skLineSegment(sketch, "E99.0.1", {"start": v(35, 20) * mm, "end": v(35, 30) * mm});
            skLineSegment(sketch, "E99.0.2", {"start": v(35, 30) * mm, "end": v(25, 30) * mm});
            skLineSegment(sketch, "E99.0.3", {"start": v(25, 30) * mm, "end": v(25, 25) * mm});
            skLineSegment(sketch, "E99.0.4", {"start": v(25, 25) * mm, "end": v(-35, 25) * mm});
            skLineSegment(sketch, "E99.0.5", {"start": v(-35, 25) * mm, "end": v(-35, 20) * mm});
            skPoint(sketch, "E100.0", {"position": v(-25, 0) * mm});
            skLineSegment(sketch, "E101", {"start": v(-25, 20) * mm, "end": v(-25, 25) * mm});
            skCircle(sketch, "E102", {"center": v(30, 25) * mm, "radius": 5 * mm});
            skCircle(sketch, "E103", {"center": v(-27.5, 22.5) * mm, "radius": 1.5 * mm});
            skCircle(sketch, "E104", {"center": v(30, 25) * mm, "radius": 3 * mm});
            skCircle(sketch, "E105", {"center": v(-27.5, 22.5) * mm, "radius": 2.5 * mm});
            skSolve(sketch);
        }
        {
            var Q0;
            {var subQ5=sQuery(id+"F10.wireOp",EDGE,"E99.0.5");Q0=makeQuery(id+"F10.imprint","IMPRINT",FACE,{"disambiguationData":[TD([[makeQuery(id+"F10.imprint","IMPRINT",EDGE,{"derivedFrom":subQ5}),1.0]])]});}
            var Q1;
            {var subQ3=sQuery(id+"F10.wireOp",EDGE,"E99.0.3");Q1=makeQuery(id+"F10.imprint","IMPRINT",FACE,{"disambiguationData":[TD([[makeQuery(id+"F10.imprint","IMPRINT",EDGE,{"derivedFrom":subQ3}),1.0]])]});}
            var Q2;
            {var subQ1=sQuery(id+"F10.wireOp",EDGE,"E99.0.2");var subQ3=sQuery(id+"F10.wireOp",EDGE,"E99.0.1");var subQ5=makeQuery(id+"F10.imprint","INTERSECT",VERTEX,{"derivedFrom":[subQ3,subQ1]});Q2=makeQuery(id+"F10.imprint","IMPRINT",FACE,{"disambiguationData":[TD([[makeQuery(id+"F10.imprint","IMPRINT",EDGE,{"disambiguationData":[TD([[subQ5,-1.0]])],"derivedFrom":subQ3}),-1.0]])]});}
            var Q3;
            {var subQ1=sQuery(id+"F10.wireOp",EDGE,"E99.0.1");var subQ3=sQuery(id+"F10.wireOp",EDGE,"E99.0.0");var subQ5=makeQuery(id+"F10.imprint","INTERSECT",VERTEX,{"derivedFrom":[subQ3,subQ1]});Q3=makeQuery(id+"F10.imprint","IMPRINT",FACE,{"disambiguationData":[TD([[makeQuery(id+"F10.imprint","IMPRINT",EDGE,{"disambiguationData":[TD([[subQ5,-1.0]])],"derivedFrom":subQ3}),-1.0]])]});}
            var Q4;
            Q4=makeQuery(id+"F10.imprint","IMPRINT",FACE,{"disambiguationData":[TD([[makeQuery(id+"F10.imprint","IMPRINT",EDGE,{"derivedFrom":sQuery(id+"F10.wireOp",EDGE,"E104")}),1.0]])]});
            var Q5;
            Q5=makeQuery(id+"F10.imprint","IMPRINT",FACE,{"disambiguationData":[TD([[makeQuery(id+"F10.imprint","IMPRINT",EDGE,{"derivedFrom":sQuery(id+"F10.wireOp",EDGE,"E103")}),1.0]])]});
            var Q6;
            Q6=makeQuery(id+"F9.boolean.opBoolean","MERGE",FACE,{"derivedFrom":[makeQuery(id+"F8.opExtrude","SWEPT_FACE",FACE,{"disambiguationData":[OSD([sQuery(id+"F0.wireOp",EDGE,"E0.bottom"),sQuery(id+"F0.wireOp",EDGE,"E26.bottom")])]}),makeQuery(id+"F9.opExtrude","SWEPT_FACE",FACE,{"disambiguationData":[OSD([sQuery(id+"F0.wireOp",EDGE,"E3.bottom")])]})]});
            extrude(context, id + "F11", {"entities" : qUnion([Q0, Q1, Q2, Q3, Q4, Q5]), "operationType" : NewBodyOperationType.REMOVE, "endBound" : BoundingType.UP_TO_SURFACE, "oppositeDirection" : true, "endBoundEntityFace" : qUnion([Q6]), "depth" : 25 * mm});
        }
        {
            var Q0;
            Q0=makeQuery(id+"F0.imprint","IMPRINT",FACE,{"disambiguationData":[TD([[makeQuery(id+"F0.imprint","IMPRINT",EDGE,{"derivedFrom":sQuery(id+"F0.wireOp",EDGE,"E29")}),1.0]])]});
            var Q1;
            Q1=makeQuery(id+"F0.imprint","IMPRINT",FACE,{"disambiguationData":[TD([[makeQuery(id+"F0.imprint","IMPRINT",EDGE,{"derivedFrom":sQuery(id+"F0.wireOp",EDGE,"E27")}),1.0]])]});
            var Q2;
            Q2=makeQuery(id+"F0.imprint","IMPRINT",FACE,{"disambiguationData":[TD([[makeQuery(id+"F0.imprint","IMPRINT",EDGE,{"derivedFrom":sQuery(id+"F0.wireOp",EDGE,"E28")}),1.0]])]});
            var Q3;
            {var subQ2=sQuery(id+"F0.wireOp",EDGE,"E26.bottom");Q3=makeQuery(id+"F0.imprint","IMPRINT",FACE,{"disambiguationData":[TD([[makeQuery(id+"F0.imprint","IMPRINT",EDGE,{"derivedFrom":subQ2}),1.0]])]});}
            var Q4;
            Q4=makeQuery(id+"F8.opExtrude","CAP_FACE",FACE,{"disambiguationData":[OSD([sQuery(id+"F0.wireOp",EDGE,"E0.bottom"),sQuery(id+"F0.wireOp",EDGE,"E0.right"),sQuery(id+"F0.wireOp",EDGE,"E4.bottom"),sQuery(id+"F0.wireOp",EDGE,"E26.bottom"),sQuery(id+"F0.wireOp",EDGE,"E26.top"),sQuery(id+"F0.wireOp",EDGE,"E26.right"),sQuery(id+"F0.wireOp",EDGE,"E27"),sQuery(id+"F0.wireOp",EDGE,"E28"),sQuery(id+"F0.wireOp",EDGE,"E29"),sQuery(id+"F0.wireOp",EDGE,"E30"),sQuery(id+"F0.wireOp",EDGE,"E31"),sQuery(id+"F0.wireOp",EDGE,"E32"),sQuery(id+"F0.wireOp",EDGE,"E33"),sQuery(id+"F0.wireOp",EDGE,"E63"),sQuery(id+"F0.wireOp",EDGE,"E64"),sQuery(id+"F0.wireOp",EDGE,"E65"),sQuery(id+"F0.wireOp",EDGE,"E70"),sQuery(id+"F0.wireOp",EDGE,"E71"),sQuery(id+"F0.wireOp",EDGE,"E72"),sQuery(id+"F0.wireOp",EDGE,"E73"),sQuery(id+"F0.wireOp",EDGE,"E74"),sQuery(id+"F0.wireOp",EDGE,"E75"),sQuery(id+"F0.wireOp",EDGE,"E76"),sQuery(id+"F0.wireOp",EDGE,"E77"),sQuery(id+"F0.wireOp",EDGE,"E78"),sQuery(id+"F0.wireOp",EDGE,"E79.filletArc"),sQuery(id+"F0.wireOp",EDGE,"E80.filletArc"),sQuery(id+"F0.wireOp",EDGE,"E81.filletArc"),sQuery(id+"F0.wireOp",EDGE,"E82.filletArc"),sQuery(id+"F0.wireOp",EDGE,"E83.filletArc"),sQuery(id+"F0.wireOp",EDGE,"E84.filletArc"),sQuery(id+"F0.wireOp",EDGE,"E85.filletArc"),sQuery(id+"F0.wireOp",EDGE,"E86.filletArc"),sQuery(id+"F0.wireOp",EDGE,"E87.filletArc"),sQuery(id+"F0.wireOp",EDGE,"E88.filletArc"),sQuery(id+"F0.wireOp",EDGE,"E89.filletArc"),sQuery(id+"F0.wireOp",EDGE,"E90.filletArc")])],"isStart":false});
            var Q5;
            {var subQ0=sQuery(id+"F0.wireOp",EDGE,"E0.right");Q5=makeQuery(id+"F9.boolean.opBoolean","MERGE",FACE,{"derivedFrom":[makeQuery(id+"F8.opExtrude","CAP_FACE",FACE,{"disambiguationData":[OSD([sQuery(id+"F0.wireOp",EDGE,"E0.bottom"),subQ0,sQuery(id+"F0.wireOp",EDGE,"E4.bottom"),sQuery(id+"F0.wireOp",EDGE,"E26.bottom"),sQuery(id+"F0.wireOp",EDGE,"E26.top"),sQuery(id+"F0.wireOp",EDGE,"E26.right"),sQuery(id+"F0.wireOp",EDGE,"E27"),sQuery(id+"F0.wireOp",EDGE,"E28"),sQuery(id+"F0.wireOp",EDGE,"E29"),sQuery(id+"F0.wireOp",EDGE,"E30"),sQuery(id+"F0.wireOp",EDGE,"E31"),sQuery(id+"F0.wireOp",EDGE,"E32"),sQuery(id+"F0.wireOp",EDGE,"E33"),sQuery(id+"F0.wireOp",EDGE,"E63"),sQuery(id+"F0.wireOp",EDGE,"E64"),sQuery(id+"F0.wireOp",EDGE,"E65"),sQuery(id+"F0.wireOp",EDGE,"E70"),sQuery(id+"F0.wireOp",EDGE,"E71"),sQuery(id+"F0.wireOp",EDGE,"E72"),sQuery(id+"F0.wireOp",EDGE,"E73"),sQuery(id+"F0.wireOp",EDGE,"E74"),sQuery(id+"F0.wireOp",EDGE,"E75"),sQuery(id+"F0.wireOp",EDGE,"E76"),sQuery(id+"F0.wireOp",EDGE,"E77"),sQuery(id+"F0.wireOp",EDGE,"E78"),sQuery(id+"F0.wireOp",EDGE,"E79.filletArc"),sQuery(id+"F0.wireOp",EDGE,"E80.filletArc"),sQuery(id+"F0.wireOp",EDGE,"E81.filletArc"),sQuery(id+"F0.wireOp",EDGE,"E82.filletArc"),sQuery(id+"F0.wireOp",EDGE,"E83.filletArc"),sQuery(id+"F0.wireOp",EDGE,"E84.filletArc"),sQuery(id+"F0.wireOp",EDGE,"E85.filletArc"),sQuery(id+"F0.wireOp",EDGE,"E86.filletArc"),sQuery(id+"F0.wireOp",EDGE,"E87.filletArc"),sQuery(id+"F0.wireOp",EDGE,"E88.filletArc"),sQuery(id+"F0.wireOp",EDGE,"E89.filletArc"),sQuery(id+"F0.wireOp",EDGE,"E90.filletArc")])],"isStart":true}),makeQuery(id+"F9.opExtrude","CAP_FACE",FACE,{"disambiguationData":[OSD([sQuery(id+"F0.wireOp",EDGE,"E3.bottom"),sQuery(id+"F0.wireOp",EDGE,"E3.top"),subQ0,sQuery(id+"F0.wireOp",EDGE,"E3.right"),sQuery(id+"F0.wireOp",EDGE,"E12"),sQuery(id+"F0.wireOp",EDGE,"E13"),sQuery(id+"F0.wireOp",EDGE,"E14"),sQuery(id+"F0.wireOp",EDGE,"E15"),sQuery(id+"F0.wireOp",EDGE,"E16"),sQuery(id+"F0.wireOp",EDGE,"E17"),sQuery(id+"F0.wireOp",EDGE,"E18")])],"isStart":true})]});}
            extrude(context, id + "F12", {"entities" : qUnion([Q0, Q1, Q2, Q3]), "operationType" : NewBodyOperationType.REMOVE, "endBound" : BoundingType.UP_TO_SURFACE, "endBoundEntityFace" : qUnion([Q4]), "depth" : 25 * mm, "hasSecondDirection" : true, "secondDirectionBound" : SecondDirectionBoundingType.UP_TO_SURFACE, "secondDirectionOppositeDirection" : false, "secondDirectionBoundEntityFace" : qUnion([Q5]), "secondDirectionDepth" : 25 * mm});
        }
        {
            var Q0;
            Q0=makeQuery(id+"F0.imprint","IMPRINT",FACE,{"disambiguationData":[TD([[makeQuery(id+"F0.imprint","IMPRINT",EDGE,{"derivedFrom":sQuery(id+"F0.wireOp",EDGE,"E16")}),-1.0]])]});
            var Q1;
            Q1=makeQuery(id+"F0.imprint","IMPRINT",FACE,{"disambiguationData":[TD([[makeQuery(id+"F0.imprint","IMPRINT",EDGE,{"derivedFrom":sQuery(id+"F0.wireOp",EDGE,"E12")}),-1.0]])]});
            var Q2;
            Q2=makeQuery(id+"F0.imprint","IMPRINT",FACE,{"disambiguationData":[TD([[makeQuery(id+"F0.imprint","IMPRINT",EDGE,{"derivedFrom":sQuery(id+"F0.wireOp",EDGE,"E13")}),-1.0]])]});
            var Q3;
            {var subQ2=sQuery(id+"F0.wireOp",EDGE,"E3.bottom");Q3=makeQuery(id+"F0.imprint","IMPRINT",FACE,{"disambiguationData":[TD([[makeQuery(id+"F0.imprint","IMPRINT",EDGE,{"derivedFrom":subQ2}),-1.0]])]});}
            extrude(context, id + "F13", {"entities" : qUnion([Q0, Q1, Q2, Q3]), "operationType" : NewBodyOperationType.REMOVE, "depth" : 30 * mm, "hasSecondDirection" : true, "secondDirectionOppositeDirection" : false, "secondDirectionDepth" : 20 * mm});
        }
        {
            var Q0;
            Q0=qCreatedBy(makeId("Front.planeOp"),FACE);
            var sketch = newSketch(context, id + "F14", { "sketchPlane" : qUnion([Q0])});
            skCircle(sketch, "E106", {"center": v(-15.45, 12.6) * mm, "radius": 1.5 * mm});
            skCircle(sketch, "E107", {"center": v(20.15, 12.69) * mm, "radius": 3 * mm});
            skSolve(sketch);
        }
        {
            var Q0;
            Q0=makeQuery(id+"F14.imprint","IMPRINT",FACE,{"disambiguationData":[TD([[makeQuery(id+"F14.imprint","IMPRINT",EDGE,{"derivedFrom":sQuery(id+"F14.wireOp",EDGE,"E106")}),1.0]])]});
            var Q1;
            Q1=makeQuery(id+"F14.imprint","IMPRINT",FACE,{"disambiguationData":[TD([[makeQuery(id+"F14.imprint","IMPRINT",EDGE,{"derivedFrom":sQuery(id+"F14.wireOp",EDGE,"E107")}),1.0]])]});
            extrude(context, id + "F15", {"entities" : qUnion([Q0, Q1]), "depth" : 25 * mm, "hasSecondDirection" : true, "secondDirectionOppositeDirection" : true, "secondDirectionDepth" : 25 * mm});
        }
    });
